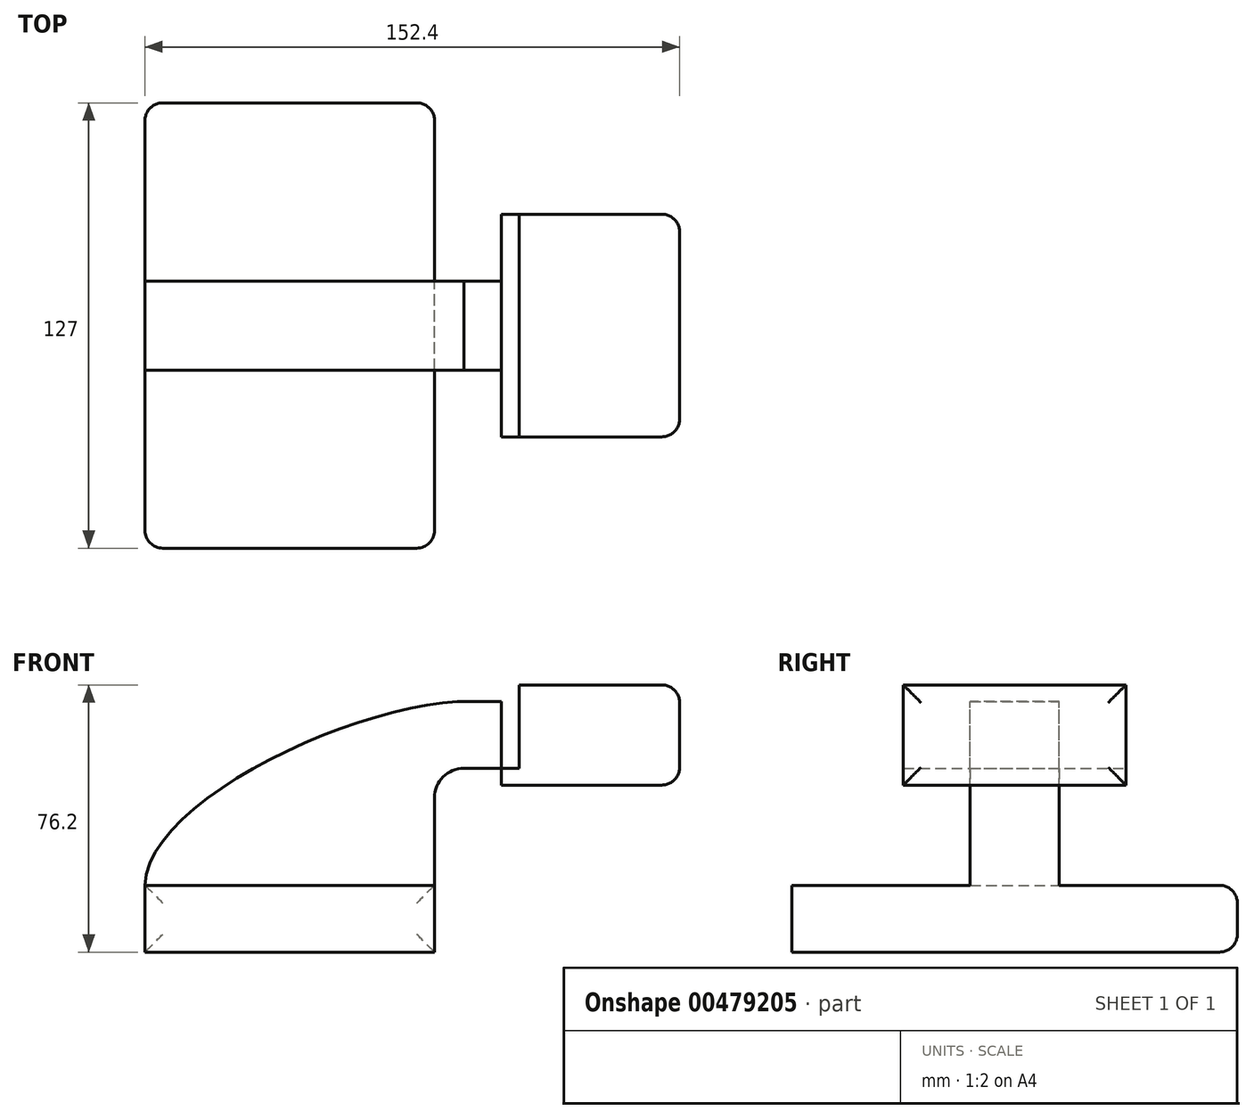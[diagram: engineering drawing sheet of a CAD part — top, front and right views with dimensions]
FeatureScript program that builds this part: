
annotation { "Feature Type Name" : "Feature", "Feature Type Description" : "" }
export const myFeature = defineFeature(function(context is Context, id is Id, definition is map)
    precondition{}
    {
        {
            var Q0;
            Q0=qCreatedBy(makeId("Front.planeOp"),FACE);
            var sketch = newSketch(context, id + "F0", { "sketchPlane" : qUnion([Q0])});
            skLineSegment(sketch, "E0.bottom", {"start": v(41.27, 9.53) * mm, "end": v(-41.28, 9.53) * mm});
            skLineSegment(sketch, "E0.top", {"start": v(41.28, -9.52) * mm, "end": v(-41.27, -9.52) * mm});
            skLineSegment(sketch, "E0.left", {"start": v(41.28, 9.53) * mm, "end": v(41.28, -9.52) * mm});
            skLineSegment(sketch, "E0.right", {"start": v(-41.28, 9.53) * mm, "end": v(-41.27, -9.52) * mm});
            skPoint(sketch, "E0.middle", {"position": v(0, 0) * mm});
            skLineSegment(sketch, "E1.bottom", {"start": v(111.12, 38.1) * mm, "end": v(60.32, 38.1) * mm});
            skLineSegment(sketch, "E1.top", {"start": v(111.12, 66.68) * mm, "end": v(60.32, 66.68) * mm});
            skLineSegment(sketch, "E1.left", {"start": v(111.12, 38.1) * mm, "end": v(111.12, 66.68) * mm});
            skLineSegment(sketch, "E1.right", {"start": v(60.32, 38.1) * mm, "end": v(60.32, 66.68) * mm});
            skPoint(sketch, "E1.middle", {"position": v(85.72, 52.39) * mm});
            skLineSegment(sketch, "E2", {"start": v(41.27, 9.53) * mm, "end": v(41.27, 34.5) * mm});
            skArc(sketch, "E3", {"start": v(41.27, 34.5) * mm, "mid": v(43.73, 40.42) * mm, "end": v(49.64, 42.88) * mm});
            skLineSegment(sketch, "E4", {"start": v(49.64, 42.88) * mm, "end": v(65.46, 42.88) * mm});
            skLineSegment(sketch, "E5.0", {"start": v(49.64, 61.93) * mm, "end": v(65.46, 61.93) * mm});
            skArc(sketch, "E5.1", {"start": v(22.22, 34.5) * mm, "mid": v(30.25, 53.9) * mm, "end": v(49.64, 61.93) * mm});
            skLineSegment(sketch, "E5.2", {"start": v(22.23, 9.53) * mm, "end": v(22.23, 34.5) * mm});
            skLineSegment(sketch, "E6", {"start": v(65.46, 61.93) * mm, "end": v(65.46, 42.88) * mm});
            skLineSegment(sketch, "E7", {"start": v(22.23, 9.53) * mm, "end": v(41.27, 9.53) * mm});
            skLineSegment(sketch, "E8", {"start": v(65.46, 52.4) * mm, "end": v(65.46, 66.68) * mm});
            skLineSegment(sketch, "E9", {"start": v(65.46, 66.68) * mm, "end": v(65.46, 42.88) * mm});
            skFitSpline(sketch, "E10", {"points": [v(-41.28, 9.52) * mm, v(49.64, 61.93) * mm], "startDerivative": vector(1.87, 72.88) * mm, "endDerivative": vector(92, 1.6) * mm});
            skSolve(sketch);
        }
        {
            var Q0;
            Q0=makeQuery(id+"F0.imprint","IMPRINT",FACE,{"disambiguationData":[TD([[makeQuery(id+"F0.imprint","IMPRINT",EDGE,{"derivedFrom":sQuery(id+"F0.wireOp",EDGE,"E0.bottom")}),1.0]])]});
            extrude(context, id + "F1", {"entities" : qUnion([Q0]), "endBound" : BoundingType.SYMMETRIC, "depth" : 127 * mm});
        }
        {
            var Q0;
            Q0=makeQuery(id+"F0.imprint","IMPRINT",FACE,{"disambiguationData":[TD([[makeQuery(id+"F0.imprint","IMPRINT",EDGE,{"derivedFrom":sQuery(id+"F0.wireOp",EDGE,"E2")}),1.0]])]});
            var Q1;
            {var subQ0=sQuery(id+"F0.wireOp",EDGE,"E0.bottom");Q1=makeQuery(id+"F0.imprint","IMPRINT",FACE,{"disambiguationData":[TD([[makeQuery(id+"F0.imprint","IMPRINT",EDGE,{"derivedFrom":subQ0}),-1.0]])]});}
            extrude(context, id + "F2", {"entities" : qUnion([Q0, Q1]), "operationType" : NewBodyOperationType.ADD, "endBound" : BoundingType.SYMMETRIC, "depth" : 25.4 * mm});
        }
        {
            var Q0;
            {var subQ1=sQuery(id+"F0.wireOp",EDGE,"E1.bottom");Q0=makeQuery(id+"F0.imprint","IMPRINT",FACE,{"disambiguationData":[TD([[makeQuery(id+"F0.imprint","IMPRINT",EDGE,{"derivedFrom":subQ1}),-1.0]])]});}
            extrude(context, id + "F3", {"entities" : qUnion([Q0]), "endBound" : BoundingType.SYMMETRIC, "depth" : 63.5 * mm});
        }
        {
            var Q0;
            Q0=makeQuery(id+"F1.opExtrude","CAP_EDGE",EDGE,{"disambiguationData":[OSD([sQuery(id+"F0.wireOp",EDGE,"E0.left")])],"isStart":false});
            var Q1;
            Q1=makeQuery(id+"F3.opExtrude","SWEPT_FACE",FACE,{"disambiguationData":[OSD([sQuery(id+"F0.wireOp",EDGE,"E1.left")])]});
            var Q2;
            Q2=makeQuery(id+"F1.opExtrude","CAP_EDGE",EDGE,{"disambiguationData":[OSD([sQuery(id+"F0.wireOp",EDGE,"E0.left")])],"isStart":true});
            var Q3;
            Q3=makeQuery(id+"F1.opExtrude","CAP_FACE",FACE,{"disambiguationData":[OSD([sQuery(id+"F0.wireOp",EDGE,"E0.bottom"),sQuery(id+"F0.wireOp",EDGE,"E0.top"),sQuery(id+"F0.wireOp",EDGE,"E0.left"),sQuery(id+"F0.wireOp",EDGE,"E0.right"),sQuery(id+"F0.wireOp",EDGE,"E7")])],"isStart":true});
            var Q4;
            Q4=makeQuery(id+"F1.opExtrude","CAP_EDGE",EDGE,{"disambiguationData":[OSD([sQuery(id+"F0.wireOp",EDGE,"E0.right")])],"isStart":false});
            fillet(context, id + "F4", {"entities" : qUnion([Q0, Q1, Q2, Q3, Q4]), "radius" : 5.08 * mm, "tangentPropagation" : true, "allowEdgeOverflow" : false});
        }
    });
